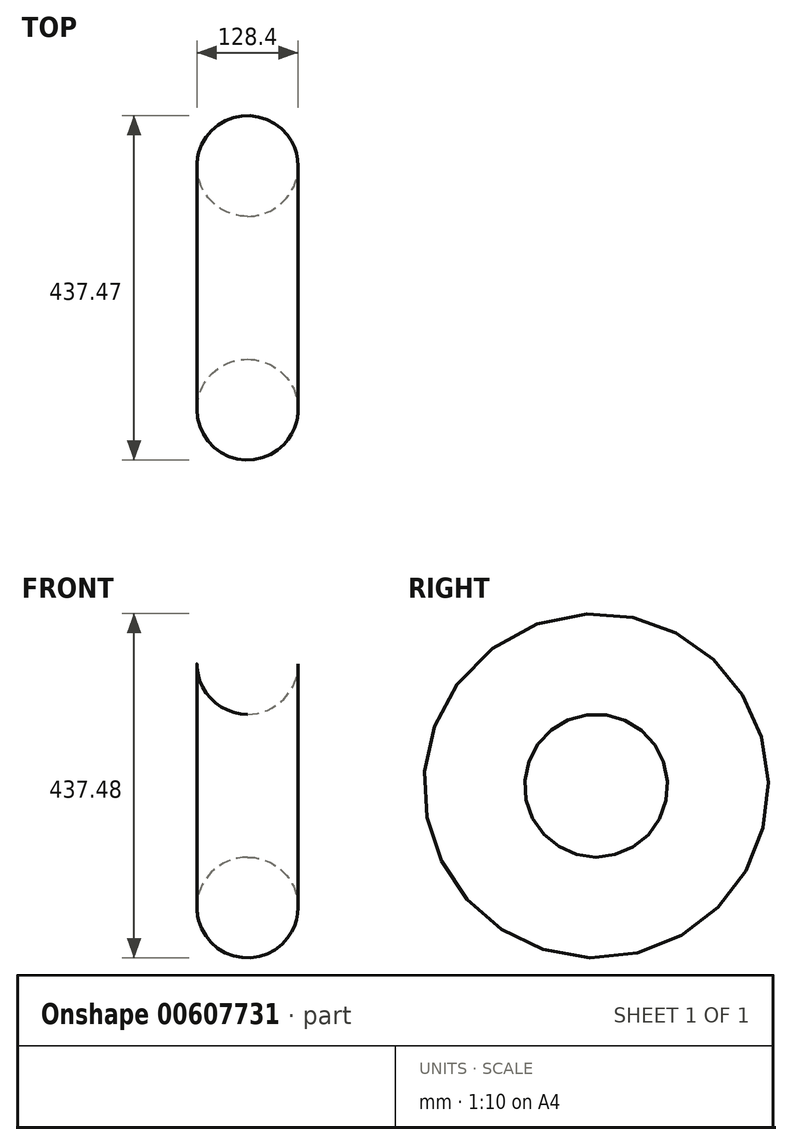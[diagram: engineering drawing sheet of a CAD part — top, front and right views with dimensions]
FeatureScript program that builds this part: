
annotation { "Feature Type Name" : "Feature", "Feature Type Description" : "" }
export const myFeature = defineFeature(function(context is Context, id is Id, definition is map)
    precondition{}
    {
        {
            var Q0;
            Q0=qCreatedBy(makeId("Front.planeOp"),FACE);
            var sketch = newSketch(context, id + "F0", { "sketchPlane" : qUnion([Q0])});
            skCircle(sketch, "E0", {"center": v(0, 0) * mm, "radius": 64.2 * mm});
            skSolve(sketch);
        }
        {
            var Q0;
            Q0=qCreatedBy(makeId("Right.planeOp"),FACE);
            var sketch = newSketch(context, id + "F1", { "sketchPlane" : qUnion([Q0])});
            skCircle(sketch, "E1", {"center": v(11.9, -154.21) * mm, "radius": 154.67 * mm});
            skSolve(sketch);
        }
        {
            var Q0;
            Q0 = qSketchRegion(id + "F0", true);
            var Q1;
            Q1=sQuery(id+"F1.wireOp",EDGE,"E1");
            revolve(context, id + "F2", {"entities" : qUnion([Q0]), "axis" : qUnion([Q1]), "revolveType" : RevolveType.FULL});
        }
    });
